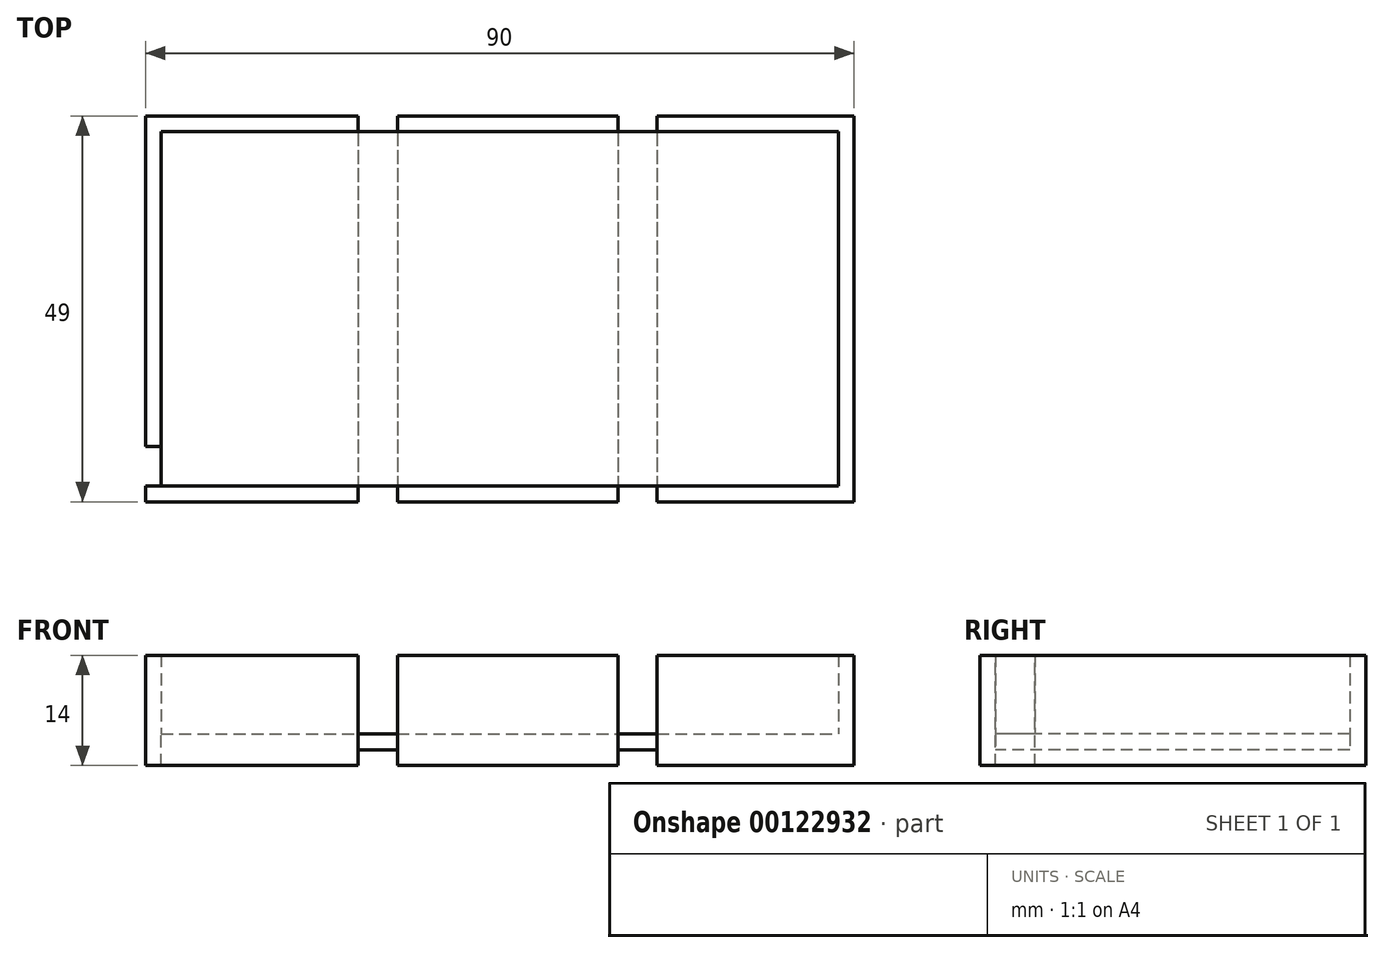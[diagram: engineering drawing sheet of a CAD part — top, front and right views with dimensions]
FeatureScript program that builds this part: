
annotation { "Feature Type Name" : "Feature", "Feature Type Description" : "" }
export const myFeature = defineFeature(function(context is Context, id is Id, definition is map)
    precondition{}
    {
        {
            var Q0;
            Q0=qCreatedBy(makeId("Top.planeOp"),FACE);
            var sketch = newSketch(context, id + "F0", { "sketchPlane" : qUnion([Q0])});
            skLineSegment(sketch, "E0.bottom", {"start": v(-43, 22.5) * mm, "end": v(43, 22.5) * mm});
            skLineSegment(sketch, "E0.top", {"start": v(-43, -22.5) * mm, "end": v(43, -22.5) * mm});
            skLineSegment(sketch, "E0.left", {"start": v(-43, 22.5) * mm, "end": v(-43, -22.5) * mm});
            skLineSegment(sketch, "E0.right", {"start": v(43, 22.5) * mm, "end": v(43, -22.5) * mm});
            skLineSegment(sketch, "E1.0", {"start": v(-45, 24.5) * mm, "end": v(-18, 24.5) * mm});
            skLineSegment(sketch, "E1.1", {"start": v(-45, 24.5) * mm, "end": v(-45, -17.5) * mm});
            skLineSegment(sketch, "E1.2", {"start": v(-45, -24.5) * mm, "end": v(-18, -24.5) * mm});
            skLineSegment(sketch, "E1.3", {"start": v(45, 24.5) * mm, "end": v(45, -24.5) * mm});
            skLineSegment(sketch, "E2", {"start": v(-18, 24.5) * mm, "end": v(-18, -24.5) * mm});
            skLineSegment(sketch, "E3", {"start": v(20, 24.5) * mm, "end": v(20, -24.5) * mm});
            skLineSegment(sketch, "E4.0", {"start": v(-13, 24.5) * mm, "end": v(-13, -24.5) * mm});
            skLineSegment(sketch, "E5.0", {"start": v(15, 24.5) * mm, "end": v(15, -24.5) * mm});
            skLineSegment(sketch, "E6.trimOffspring", {"start": v(-13, 24.5) * mm, "end": v(15, 24.5) * mm});
            skLineSegment(sketch, "E7.trimOffspring", {"start": v(20, 24.5) * mm, "end": v(45, 24.5) * mm});
            skLineSegment(sketch, "E8.trimOffspring", {"start": v(20, -24.5) * mm, "end": v(45, -24.5) * mm});
            skLineSegment(sketch, "E9.trimOffspring", {"start": v(-13, -24.5) * mm, "end": v(15, -24.5) * mm});
            skLineSegment(sketch, "E10", {"start": v(-43, -22.5) * mm, "end": v(-45, -22.5) * mm});
            skLineSegment(sketch, "E11.0", {"start": v(-43, -17.5) * mm, "end": v(-45, -17.5) * mm});
            skLineSegment(sketch, "E12.trimOffspring", {"start": v(-45, -22.5) * mm, "end": v(-45, -24.5) * mm});
            skSolve(sketch);
        }
        {
            var Q0;
            {var subQ0=sQuery(id+"F0.wireOp",EDGE,"E0.left");var subQ4=sQuery(id+"F0.wireOp",EDGE,"E0.bottom");var subQ5=makeQuery(id+"F0.imprint","INTERSECT",VERTEX,{"derivedFrom":[subQ4,subQ0]});Q0=makeQuery(id+"F0.imprint","IMPRINT",FACE,{"disambiguationData":[TD([[makeQuery(id+"F0.imprint","IMPRINT",EDGE,{"disambiguationData":[TD([[subQ5,-1.0]])],"derivedFrom":subQ4}),-1.0]])]});}
            var Q1;
            {var subQ0=sQuery(id+"F0.wireOp",EDGE,"E4.0");var subQ1=sQuery(id+"F0.wireOp",EDGE,"E0.bottom");var subQ2=makeQuery(id+"F0.imprint","INTERSECT",VERTEX,{"derivedFrom":[subQ1,subQ0]});Q1=makeQuery(id+"F0.imprint","IMPRINT",FACE,{"disambiguationData":[TD([[makeQuery(id+"F0.imprint","IMPRINT",EDGE,{"disambiguationData":[TD([[subQ2,-1.0]])],"derivedFrom":subQ1}),-1.0]])]});}
            var Q2;
            {var subQ0=sQuery(id+"F0.wireOp",EDGE,"E0.right");Q2=makeQuery(id+"F0.imprint","IMPRINT",FACE,{"disambiguationData":[TD([[makeQuery(id+"F0.imprint","IMPRINT",EDGE,{"derivedFrom":subQ0}),-1.0]])]});}
            var Q3;
            {var subQ2=sQuery(id+"F0.wireOp",EDGE,"E1.2");Q3=makeQuery(id+"F0.imprint","IMPRINT",FACE,{"disambiguationData":[TD([[makeQuery(id+"F0.imprint","IMPRINT",EDGE,{"derivedFrom":subQ2}),1.0]])]});}
            var Q4;
            {var subQ5=sQuery(id+"F0.wireOp",EDGE,"E9.trimOffspring");Q4=makeQuery(id+"F0.imprint","IMPRINT",FACE,{"disambiguationData":[TD([[makeQuery(id+"F0.imprint","IMPRINT",EDGE,{"derivedFrom":subQ5}),1.0]])]});}
            var Q5;
            {var subQ0=sQuery(id+"F0.wireOp",EDGE,"E0.right");Q5=makeQuery(id+"F0.imprint","IMPRINT",FACE,{"disambiguationData":[TD([[makeQuery(id+"F0.imprint","IMPRINT",EDGE,{"derivedFrom":subQ0}),1.0]])]});}
            var Q6;
            {var subQ5=sQuery(id+"F0.wireOp",EDGE,"E6.trimOffspring");Q6=makeQuery(id+"F0.imprint","IMPRINT",FACE,{"disambiguationData":[TD([[makeQuery(id+"F0.imprint","IMPRINT",EDGE,{"derivedFrom":subQ5}),-1.0]])]});}
            var Q7;
            {var subQ0=sQuery(id+"F0.wireOp",EDGE,"E1.0");Q7=makeQuery(id+"F0.imprint","IMPRINT",FACE,{"disambiguationData":[TD([[makeQuery(id+"F0.imprint","IMPRINT",EDGE,{"derivedFrom":subQ0}),-1.0]])]});}
            extrude(context, id + "F1", {"entities" : qUnion([Q0, Q1, Q2, Q3, Q4, Q5, Q6, Q7]), "oppositeDirection" : true, "depth" : 2 * mm, "offsetDistance" : 25 * mm});
        }
        {
            var Q0;
            {var subQ0=sQuery(id+"F0.wireOp",EDGE,"E0.right");Q0=makeQuery(id+"F0.imprint","IMPRINT",FACE,{"disambiguationData":[TD([[makeQuery(id+"F0.imprint","IMPRINT",EDGE,{"derivedFrom":subQ0}),-1.0]])]});}
            var Q1;
            {var subQ0=sQuery(id+"F0.wireOp",EDGE,"E4.0");var subQ1=sQuery(id+"F0.wireOp",EDGE,"E0.bottom");var subQ2=makeQuery(id+"F0.imprint","INTERSECT",VERTEX,{"derivedFrom":[subQ1,subQ0]});Q1=makeQuery(id+"F0.imprint","IMPRINT",FACE,{"disambiguationData":[TD([[makeQuery(id+"F0.imprint","IMPRINT",EDGE,{"disambiguationData":[TD([[subQ2,-1.0]])],"derivedFrom":subQ1}),-1.0]])]});}
            var Q2;
            {var subQ0=sQuery(id+"F0.wireOp",EDGE,"E0.left");var subQ4=sQuery(id+"F0.wireOp",EDGE,"E0.bottom");var subQ5=makeQuery(id+"F0.imprint","INTERSECT",VERTEX,{"derivedFrom":[subQ4,subQ0]});Q2=makeQuery(id+"F0.imprint","IMPRINT",FACE,{"disambiguationData":[TD([[makeQuery(id+"F0.imprint","IMPRINT",EDGE,{"disambiguationData":[TD([[subQ5,-1.0]])],"derivedFrom":subQ4}),-1.0]])]});}
            var Q3;
            {var subQ0=sQuery(id+"F0.wireOp",EDGE,"E2");var subQ1=sQuery(id+"F0.wireOp",EDGE,"E0.bottom");var subQ2=makeQuery(id+"F0.imprint","INTERSECT",VERTEX,{"derivedFrom":[subQ1,subQ0]});Q3=makeQuery(id+"F0.imprint","IMPRINT",FACE,{"disambiguationData":[TD([[makeQuery(id+"F0.imprint","IMPRINT",EDGE,{"disambiguationData":[TD([[subQ2,-1.0]])],"derivedFrom":subQ1}),-1.0]])]});}
            var Q4;
            {var subQ0=sQuery(id+"F0.wireOp",EDGE,"E5.0");var subQ1=sQuery(id+"F0.wireOp",EDGE,"E0.bottom");var subQ2=makeQuery(id+"F0.imprint","INTERSECT",VERTEX,{"derivedFrom":[subQ1,subQ0]});Q4=makeQuery(id+"F0.imprint","IMPRINT",FACE,{"disambiguationData":[TD([[makeQuery(id+"F0.imprint","IMPRINT",EDGE,{"disambiguationData":[TD([[subQ2,-1.0]])],"derivedFrom":subQ1}),-1.0]])]});}
            extrude(context, id + "F2", {"entities" : qUnion([Q0, Q1, Q2, Q3, Q4]), "operationType" : NewBodyOperationType.ADD, "depth" : 2 * mm, "offsetDistance" : 25 * mm});
        }
        {
            var Q0;
            {var subQ0=sQuery(id+"F0.wireOp",EDGE,"E1.0");Q0=makeQuery(id+"F0.imprint","IMPRINT",FACE,{"disambiguationData":[TD([[makeQuery(id+"F0.imprint","IMPRINT",EDGE,{"derivedFrom":subQ0}),-1.0]])]});}
            var Q1;
            {var subQ2=sQuery(id+"F0.wireOp",EDGE,"E1.2");Q1=makeQuery(id+"F0.imprint","IMPRINT",FACE,{"disambiguationData":[TD([[makeQuery(id+"F0.imprint","IMPRINT",EDGE,{"derivedFrom":subQ2}),1.0]])]});}
            var Q2;
            {var subQ5=sQuery(id+"F0.wireOp",EDGE,"E9.trimOffspring");Q2=makeQuery(id+"F0.imprint","IMPRINT",FACE,{"disambiguationData":[TD([[makeQuery(id+"F0.imprint","IMPRINT",EDGE,{"derivedFrom":subQ5}),1.0]])]});}
            var Q3;
            {var subQ5=sQuery(id+"F0.wireOp",EDGE,"E6.trimOffspring");Q3=makeQuery(id+"F0.imprint","IMPRINT",FACE,{"disambiguationData":[TD([[makeQuery(id+"F0.imprint","IMPRINT",EDGE,{"derivedFrom":subQ5}),-1.0]])]});}
            var Q4;
            {var subQ0=sQuery(id+"F0.wireOp",EDGE,"E0.right");Q4=makeQuery(id+"F0.imprint","IMPRINT",FACE,{"disambiguationData":[TD([[makeQuery(id+"F0.imprint","IMPRINT",EDGE,{"derivedFrom":subQ0}),1.0]])]});}
            extrude(context, id + "F3", {"entities" : qUnion([Q0, Q1, Q2, Q3, Q4]), "operationType" : NewBodyOperationType.ADD, "depth" : 12 * mm, "offsetDistance" : 25 * mm});
        }
    });
